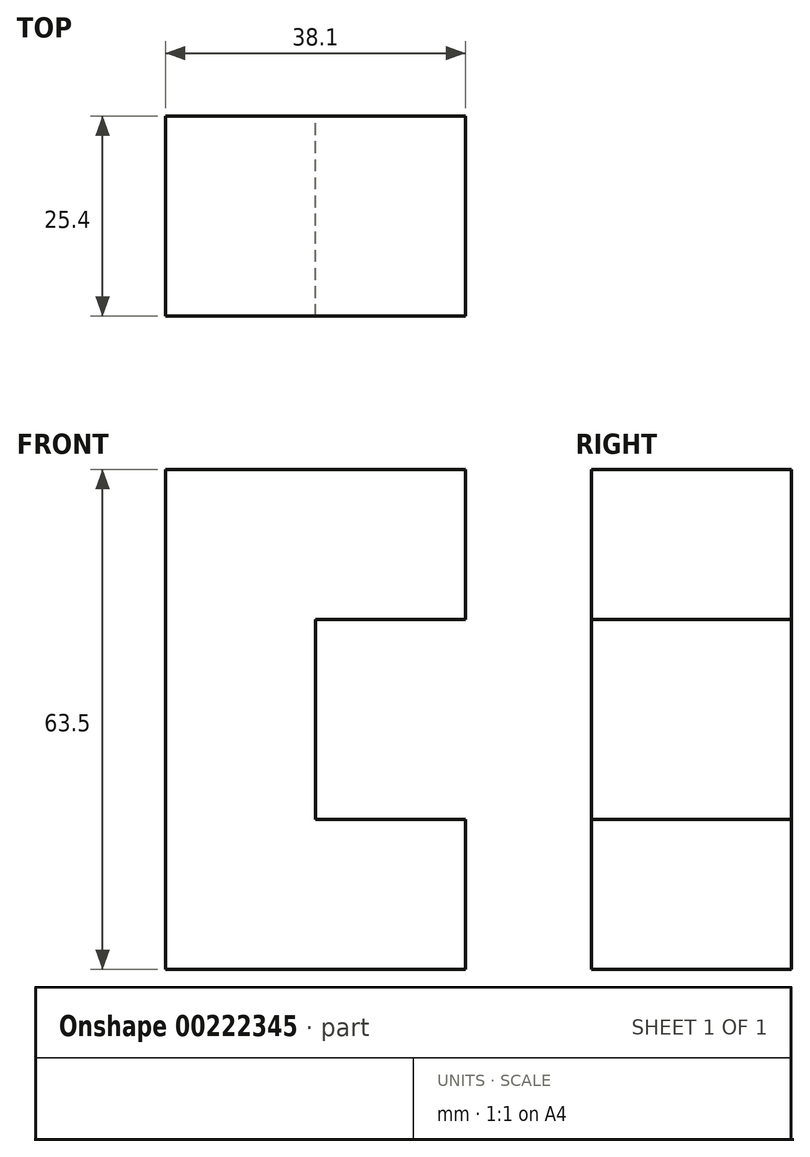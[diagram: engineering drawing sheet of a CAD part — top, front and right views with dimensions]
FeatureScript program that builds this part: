
annotation { "Feature Type Name" : "Feature", "Feature Type Description" : "" }
export const myFeature = defineFeature(function(context is Context, id is Id, definition is map)
    precondition{}
    {
        {
            var Q0;
            Q0=qCreatedBy(makeId("Front.planeOp"),FACE);
            var sketch = newSketch(context, id + "F0", { "sketchPlane" : qUnion([Q0])});
            skLineSegment(sketch, "E0.bottom", {"start": v(-43.35, 10.96) * mm, "end": v(-62.4, 10.96) * mm});
            skLineSegment(sketch, "E0.top", {"start": v(-43.35, 74.46) * mm, "end": v(-62.4, 74.46) * mm});
            skLineSegment(sketch, "E0.left", {"start": v(-43.35, 10.96) * mm, "end": v(-43.35, 74.46) * mm});
            skLineSegment(sketch, "E0.right", {"start": v(-62.4, 10.96) * mm, "end": v(-62.4, 74.46) * mm});
            skPoint(sketch, "E0.middle", {"position": v(-52.87, 42.71) * mm});
            skLineSegment(sketch, "E1.bottom", {"start": v(-24.3, 55.41) * mm, "end": v(-43.35, 55.41) * mm});
            skLineSegment(sketch, "E1.top", {"start": v(-24.3, 74.46) * mm, "end": v(-43.35, 74.46) * mm});
            skLineSegment(sketch, "E1.left", {"start": v(-24.3, 55.41) * mm, "end": v(-24.3, 74.46) * mm});
            skLineSegment(sketch, "E1.right", {"start": v(-43.35, 55.41) * mm, "end": v(-43.35, 74.46) * mm});
            skPoint(sketch, "E1.middle", {"position": v(-33.82, 64.94) * mm});
            skLineSegment(sketch, "E2.bottom", {"start": v(-24.3, 10.96) * mm, "end": v(-43.35, 10.96) * mm});
            skLineSegment(sketch, "E2.top", {"start": v(-24.3, 30.01) * mm, "end": v(-43.35, 30.01) * mm});
            skLineSegment(sketch, "E2.left", {"start": v(-24.3, 10.96) * mm, "end": v(-24.3, 30.01) * mm});
            skLineSegment(sketch, "E2.right", {"start": v(-43.35, 10.96) * mm, "end": v(-43.35, 30.01) * mm});
            skPoint(sketch, "E2.middle", {"position": v(-33.82, 20.49) * mm});
            skSolve(sketch);
        }
        {
            var Q0;
            Q0=qSketchRegion(id+"F0",true);
            extrude(context, id + "F1", {"entities" : qUnion([Q0]), "endBound" : BoundingType.SYMMETRIC, "depth" : 25.4 * mm});
        }
    });
